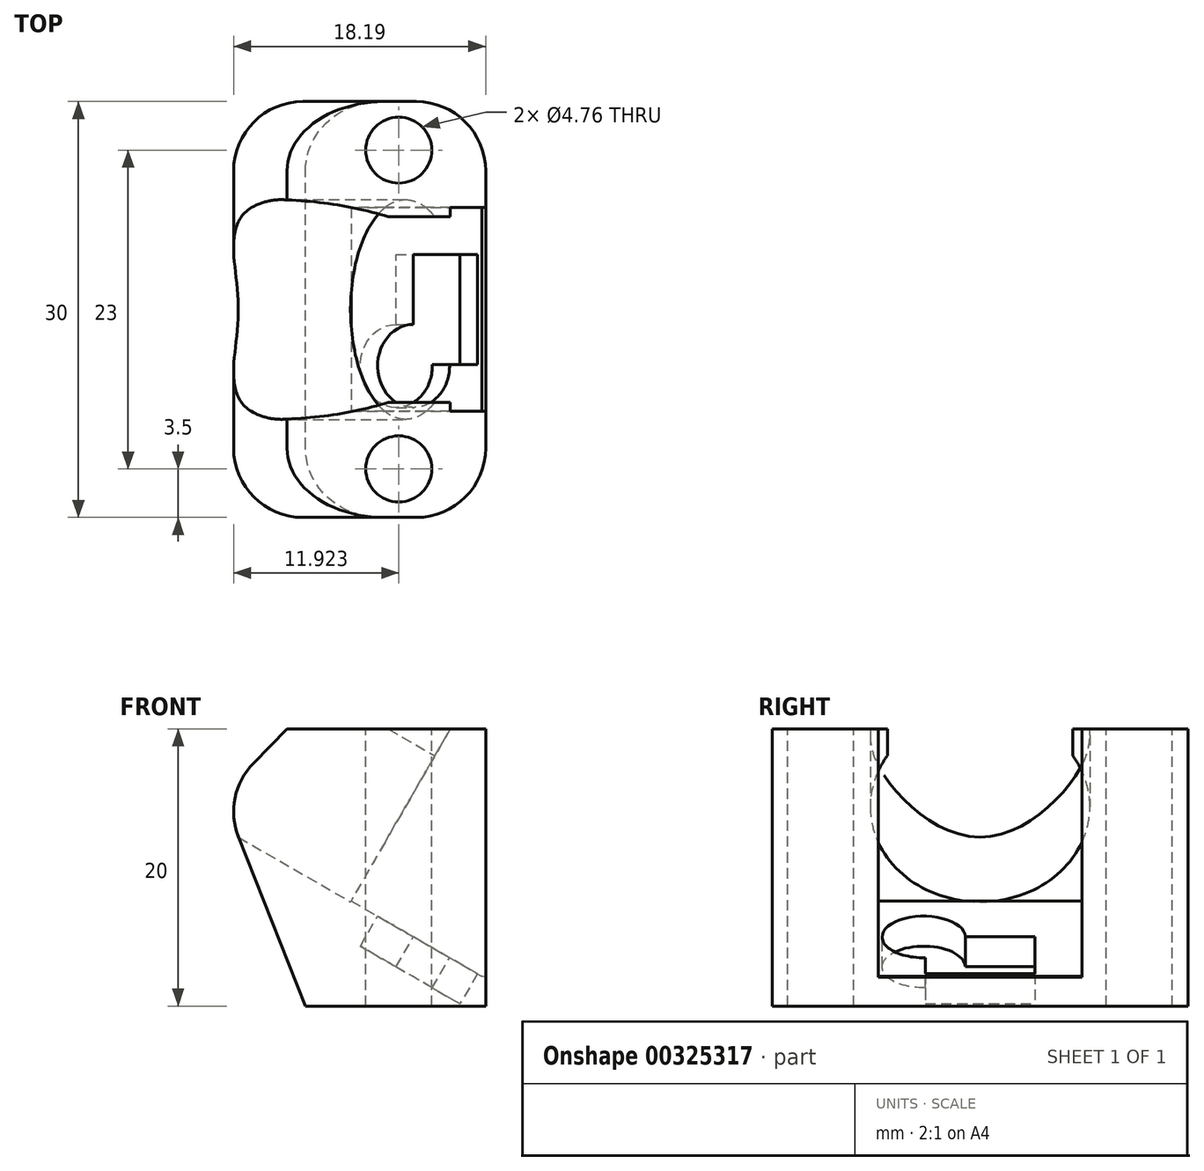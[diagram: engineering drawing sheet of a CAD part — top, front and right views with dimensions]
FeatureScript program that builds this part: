
annotation { "Feature Type Name" : "Feature", "Feature Type Description" : "" }
export const myFeature = defineFeature(function(context is Context, id is Id, definition is map)
    precondition{}
    {
        {
            var Q0;
            Q0=qCreatedBy(makeId("Front.planeOp"),FACE);
            var sketch = newSketch(context, id + "F0", { "sketchPlane" : qUnion([Q0])});
            skLineSegment(sketch, "E0", {"start": v(0, -10.8) * mm, "end": v(-13, -10.8) * mm});
            skLineSegment(sketch, "E1", {"start": v(-13, -10.8) * mm, "end": v(-19.04, 4.4) * mm});
            skLineSegment(sketch, "E2", {"start": v(0, -10.8) * mm, "end": v(0, 9.2) * mm});
            skLineSegment(sketch, "E3", {"start": v(0, 9.2) * mm, "end": v(-14.33, 9.2) * mm});
            skLineSegment(sketch, "E4", {"start": v(-14.33, 9.2) * mm, "end": v(-19.04, 4.4) * mm});
            skLineSegment(sketch, "E5", {"start": v(7.44, 0) * mm, "end": v(7.44, -10.8) * mm, "construction": true});
            skLineSegment(sketch, "E6", {"start": v(7.44, -10.8) * mm, "end": v(0, -10.8) * mm, "construction": true});
            skSolve(sketch);
        }
        {
            var Q0;
            Q0=qSketchRegion(id+"F0",true);
            extrude(context, id + "F1", {"entities" : qUnion([Q0]), "depth" : 15 * mm, "hasSecondDirection" : true, "secondDirectionOppositeDirection" : true, "secondDirectionDepth" : 15 * mm});
        }
        {
            var Q0;
            Q0=qCreatedBy(makeId("Top.planeOp"),FACE);
            cPlane(context, id + "F2", {"entities" : qUnion([Q0]), "cplaneType" : CPlaneType.OFFSET, "offset" : 5 * mm, "oppositeDirection" : true, "width" : 150 * mm, "height" : 150 * mm});
        }
        {
            var Q0;
            Q0=qCreatedBy(id+"F2.planeOp",FACE);
            var sketch = newSketch(context, id + "F3", { "sketchPlane" : qUnion([Q0])});
            skLineSegment(sketch, "E7", {"start": v(0, 7.29) * mm, "end": v(0, -6.72) * mm, "construction": true});
            skSolve(sketch);
        }
        {
            var Q0;
            Q0=qCreatedBy(id+"F2.planeOp",FACE);
            var Q1;
            Q1=qBodyType(qCreatedBy(id+"F3",EDGE),BodyType.WIRE);
            cPlane(context, id + "F4", {"entities" : qUnion([Q0, Q1]), "cplaneType" : CPlaneType.LINE_ANGLE, "offset" : 25 * mm, "angle" : 60 * degree, "width" : 150 * mm, "height" : 150 * mm});
        }
        {
            var Q0;
            Q0=qCreatedBy(makeId("Top.planeOp"),FACE);
            var sketch = newSketch(context, id + "F5", { "sketchPlane" : qUnion([Q0])});
            skLineSegment(sketch, "E8", {"start": v(-6.27, 0) * mm, "end": v(-6.27, -11.5) * mm, "construction": true});
            skLineSegment(sketch, "E9", {"start": v(-6.27, 0) * mm, "end": v(-6.27, 11.5) * mm, "construction": true});
            skCircle(sketch, "E10", {"center": v(-6.27, -11.5) * mm, "radius": 2.38 * mm});
            skCircle(sketch, "E11", {"center": v(-6.27, 11.5) * mm, "radius": 2.38 * mm});
            skSolve(sketch);
        }
        {
            var Q0;
            Q0=makeQuery(id+"F1.opExtrude","SWEPT_EDGE",EDGE,{"disambiguationData":[OSD([sQuery(id+"F0.wireOp",EDGE,"E1"),sQuery(id+"F0.wireOp",EDGE,"E4")])]});
            var Q1;
            Q1=makeQuery(id+"F1.opExtrude","CAP_EDGE",EDGE,{"disambiguationData":[OSD([sQuery(id+"F0.wireOp",EDGE,"E1")])],"isStart":false});
            var Q2;
            Q2=makeQuery(id+"F1.opExtrude","CAP_EDGE",EDGE,{"disambiguationData":[OSD([sQuery(id+"F0.wireOp",EDGE,"E1")])],"isStart":true});
            var Q3;
            Q3=makeQuery(id+"F1.opExtrude","CAP_EDGE",EDGE,{"disambiguationData":[OSD([sQuery(id+"F0.wireOp",EDGE,"E4")])],"isStart":false});
            var Q4;
            Q4=makeQuery(id+"F1.opExtrude","CAP_EDGE",EDGE,{"disambiguationData":[OSD([sQuery(id+"F0.wireOp",EDGE,"E4")])],"isStart":true});
            var Q5;
            Q5=makeQuery(id+"F1.opExtrude","CAP_EDGE",EDGE,{"disambiguationData":[OSD([sQuery(id+"F0.wireOp",EDGE,"E2")])],"isStart":false});
            var Q6;
            Q6=makeQuery(id+"F1.opExtrude","CAP_EDGE",EDGE,{"disambiguationData":[OSD([sQuery(id+"F0.wireOp",EDGE,"E2")])],"isStart":true});
            var Q7;
            Q7=makeQuery(id+"F1.opExtrude","CAP_EDGE",EDGE,{"disambiguationData":[OSD([sQuery(id+"F0.wireOp",EDGE,"E2")])],"isStart":true});
            fillet(context, id + "F6", {"entities" : qUnion([Q0, Q1, Q2, Q3, Q4, Q5, Q6, Q7]), "radius" : 5 * mm, "tangentPropagation" : true, "allowEdgeOverflow" : false});
        }
        {
            var Q0;
            Q0=qSketchRegion(id+"F5",true);
            extrude(context, id + "F7", {"entities" : qUnion([Q0]), "operationType" : NewBodyOperationType.REMOVE, "oppositeDirection" : true, "depth" : 25 * mm, "hasSecondDirection" : true, "secondDirectionOppositeDirection" : false, "secondDirectionDepth" : 25 * mm});
        }
        {
            var Q0;
            Q0=qCreatedBy(id+"F4.planeOp",FACE);
            var sketch = newSketch(context, id + "F8", { "sketchPlane" : qUnion([Q0])});
            skArc(sketch, "E12", {"start": v(-6.7, 4.45) * mm, "mid": v(0, -7.72) * mm, "end": v(6.7, 4.45) * mm});
            skPoint(sketch, "E13", {"position": v(6.7, 4.45) * mm});
            skPoint(sketch, "E14", {"position": v(-6.7, 4.45) * mm});
            skLineSegment(sketch, "E15", {"start": v(6.7, 4.45) * mm, "end": v(6.7, 12.02) * mm});
            skLineSegment(sketch, "E16", {"start": v(6.7, 12.02) * mm, "end": v(-6.7, 12.02) * mm});
            skLineSegment(sketch, "E17", {"start": v(-6.7, 12.02) * mm, "end": v(-6.7, 4.45) * mm});
            skSolve(sketch);
        }
        {
            var Q0;
            Q0=qCreatedBy(id+"F4.planeOp",FACE);
            var sketch = newSketch(context, id + "F9", { "sketchPlane" : qUnion([Q0])});
            skLineSegment(sketch, "E18.top", {"start": v(7.35, -7.64) * mm, "end": v(-7.35, -7.64) * mm});
            skLineSegment(sketch, "E18.left", {"start": v(7.35, 8.05) * mm, "end": v(7.35, -7.64) * mm});
            skLineSegment(sketch, "E18.right", {"start": v(-7.35, 8.05) * mm, "end": v(-7.35, -7.64) * mm});
            skPoint(sketch, "E18.middle", {"position": v(0, 0.2) * mm});
            skLineSegment(sketch, "E19", {"start": v(7.35, 8.05) * mm, "end": v(7.35, 12.6) * mm});
            skLineSegment(sketch, "E20", {"start": v(7.35, 12.6) * mm, "end": v(-7.35, 12.6) * mm});
            skLineSegment(sketch, "E21", {"start": v(-7.35, 12.6) * mm, "end": v(-7.35, 8.05) * mm});
            skSolve(sketch);
        }
        {
            var Q0;
            Q0 = qSketchRegion(id + "F9", true);
            extrude(context, id + "F10", {"entities" : qUnion([Q0]), "operationType" : NewBodyOperationType.REMOVE, "oppositeDirection" : true, "depth" : 9.3 * mm, "hasSecondDirection" : true, "secondDirectionOppositeDirection" : true, "secondDirectionDepth" : 0 * mm});
        }
        {
            var Q0;
            Q0 = qSketchRegion(id + "F8", true);
            extrude(context, id + "F11", {"entities" : qUnion([Q0]), "operationType" : NewBodyOperationType.REMOVE, "oppositeDirection" : true, "depth" : 25 * mm, "hasSecondDirection" : true, "secondDirectionOppositeDirection" : true, "secondDirectionDepth" : 9.3 * mm});
        }
        {
            var Q0;
            Q0=makeQuery(id+"F10.boolean.opBoolean","INTERSECT",EDGE,{"derivedFrom":[makeQuery(id+"F1.opExtrude","SWEPT_FACE",FACE,{"disambiguationData":[OSD([sQuery(id+"F0.wireOp",EDGE,"E2")])]}),makeQuery(id+"F10.opExtrude","CAP_FACE",FACE,{"disambiguationData":[OSD([sQuery(id+"F9.wireOp",EDGE,"E18.top"),sQuery(id+"F9.wireOp",EDGE,"E18.left"),sQuery(id+"F9.wireOp",EDGE,"E18.right"),sQuery(id+"F9.wireOp",EDGE,"E19"),sQuery(id+"F9.wireOp",EDGE,"E20"),sQuery(id+"F9.wireOp",EDGE,"E21")])],"isStart":true})]});
            chamfer(context, id + "F12", {"entities" : qUnion([Q0]), "width" : 1 * mm, "tangentPropagation" : true});
        }
        {
            var Q0;
            {var subQ1=sQuery(id+"F9.wireOp",EDGE,"E19");var subQ2=sQuery(id+"F9.wireOp",EDGE,"E18.left");var subQ3=sQuery(id+"F9.wireOp",EDGE,"E18.top");var subQ4=makeQuery(id+"F10.boolean.opBoolean","COPY",FACE,{"derivedFrom":makeQuery(id+"F10.opExtrude","CAP_FACE",FACE,{"disambiguationData":[OSD([subQ3,subQ2,sQuery(id+"F9.wireOp",EDGE,"E18.right"),subQ1,sQuery(id+"F9.wireOp",EDGE,"E20"),sQuery(id+"F9.wireOp",EDGE,"E21")])],"isStart":false})});var subQ5=makeQuery(id+"F10.boolean.opBoolean","COPY",FACE,{"derivedFrom":makeQuery(id+"F10.opExtrude","SWEPT_FACE",FACE,{"disambiguationData":[OSD([subQ3])]})});Q0=makeQuery(id+"F11.boolean.opBoolean","SPLIT",EDGE,{"disambiguationData":[topologyDisambiguationEdgeConnected([subQ5,subQ4]),TD([makeQuery(id+"F10.boolean.opBoolean","COPY",FACE,{"derivedFrom":makeQuery(id+"F10.opExtrude","SWEPT_FACE",FACE,{"disambiguationData":[OSD([subQ2,subQ1])]})})])],"derivedFrom":makeQuery(id+"F10.boolean.opBoolean","COPY",EDGE,{"derivedFrom":makeQuery(id+"F10.opExtrude","CAP_EDGE",EDGE,{"disambiguationData":[OSD([subQ3])],"isStart":false})})});}
            cPlane(context, id + "F13", {"entities" : qUnion([Q0]), "cplaneType" : CPlaneType.LINE_ANGLE, "offset" : 25 * mm, "angle" : 330 * degree, "width" : 150 * mm, "height" : 150 * mm});
        }
        {
            var Q0;
            Q0=qCreatedBy(id+"F13.planeOp",FACE);
            var sketch = newSketch(context, id + "F14", { "sketchPlane" : qUnion([Q0])});
            skCircle(sketch, "E22", {"center": v(-1.6, 4.07) * mm, "radius": 3 * mm});
            skSolve(sketch);
        }
        {
            var Q0;
            Q0=qCreatedBy(id+"F13.planeOp",FACE);
            var sketch = newSketch(context, id + "F15", { "sketchPlane" : qUnion([Q0])});
            skLineSegment(sketch, "E23", {"start": v(2.5, 0) * mm, "end": v(1.05, 0) * mm, "construction": true});
            skLineSegment(sketch, "E24.bottom", {"start": v(-1.62, 3.96) * mm, "end": v(3.72, 3.96) * mm});
            skLineSegment(sketch, "E24.top", {"start": v(-1.62, -3.96) * mm, "end": v(3.72, -3.96) * mm});
            skLineSegment(sketch, "E24.left", {"start": v(-1.62, 3.96) * mm, "end": v(-1.62, -3.96) * mm});
            skLineSegment(sketch, "E24.right", {"start": v(3.72, 3.96) * mm, "end": v(3.72, -3.96) * mm});
            skPoint(sketch, "E24.middle", {"position": v(1.05, 0) * mm});
            skSolve(sketch);
        }
        {
            var Q0;
            Q0 = qSketchRegion(id + "F14", true);
            extrude(context, id + "F16", {"entities" : qUnion([Q0]), "operationType" : NewBodyOperationType.REMOVE, "depth" : 2.5 * mm});
        }
        {
            var Q0;
            Q0 = qSketchRegion(id + "F15", true);
            extrude(context, id + "F17", {"entities" : qUnion([Q0]), "operationType" : NewBodyOperationType.REMOVE, "oppositeDirection" : true, "depth" : 25 * mm, "hasSecondDirection" : true, "secondDirectionOppositeDirection" : false, "secondDirectionDepth" : 2.5 * mm});
        }
    });
